# Revit family: Electronics_Desono_Biamp_Two-Way-High-Efficiency-Loudspeaker_DX-IC6
name_source: partatom
category: Communication Devices
units: mm (PartAtom-declared; Revit-internal decimal feet)

## family parameters
Cut with Voids When Loaded = No
Host = Face
Maintain Annotation Orientation = No
OmniClass Number = 23.85.10.11.14.14.14
OmniClass Title = Loudspeakers
Part Type = Normal
Room Calculation Point = No
Round Connector Dimension = Use Diameter
Shared = No

## types (2) — shared parameters
Autoformer = 70 V: 60 W, 30 W, 15 W, 7.5 W; 100 V: 60 W, 30 W, 15 W
Certifcations = ETL listed to comply with UL1480A, UL2043 and CSA62368-1 Suitable for use in air handling spaces per NFPA 70 and NFPA 90
Connector Description = 4-way Euroblock; Low impedance 8 ohms, 70/100V operation
Controls = Front-face wattage / low impedance selector switch
Crossover Frequency = 1.2 kHz
Default Elevation = 4' - 0"
Depth = 0' - 6 1/2"
Description = Desono™ DX-IC6 Two-Way 6.5-Inch High Efficiency Ceiling Mount Loudspeaker
Diameter = 0' - 11 1/2"
Housing Material = Biamp - Plastic - Black
Input Connection = 4-position Euroblock connector
Manufacturer = Biamp
Mounting Provisions = 3 SpringLock mounting clamps with 2.5-inch grip range
Nominal Beamwidth (H x V) = 140°, conical
Nominal Continuous Power = Passive - 28 V; (120 W @ 6.5 Ω)
Nominal Maximum SPL = Passive: Peak - 120dB; Continuous - 114dB
Operating Environment = Indoor
Operating Mode = Passive with DSP
Operating Range (-10dB) = 90 Hz to 20 kHz
Product Documentation Link = https://downloads.biamp.com
Product Page URL = https://www.biamp.com
Product data url = https://www.bimobject.com
Rated Continuous Voltage = Passive: 22.4 V; (27 dBV)
Rated Maximum SPL (Processed) = Passive: Peak - 124dB; Continuous - 112dB
Recommended Amplifers = Passive: 120 W - 240 W into 8 Ω, (31 V - 44 V)
Required Accessory = 65 Hz, 12 dB/oct. high pass flter
Sensitivity = 95 dB (2.83 V); 94 dB (1 W at rated impedance 6.5 Ω)
Shipping Weight = 30.32 lb
Transducers = LF 1 x 6.5 (165 mm); HF 1 x 1.0 (25 mm) exit compression driver
URL = https://www.biamp.com
Weight = 8.00 lb

## per-type parameters (varying)
| type | Grill Material |
| DX-IC6-W | Biamp - Plastic - White(Grid) |
| DX-IC6-B | Biamp - Plastic - Black(Grid) |

note: column(s) folded — value = type name in every type: Model

## geometry (parser evidence)
native form markers: Sweep x8
no freeform markers — native parametric forms only
